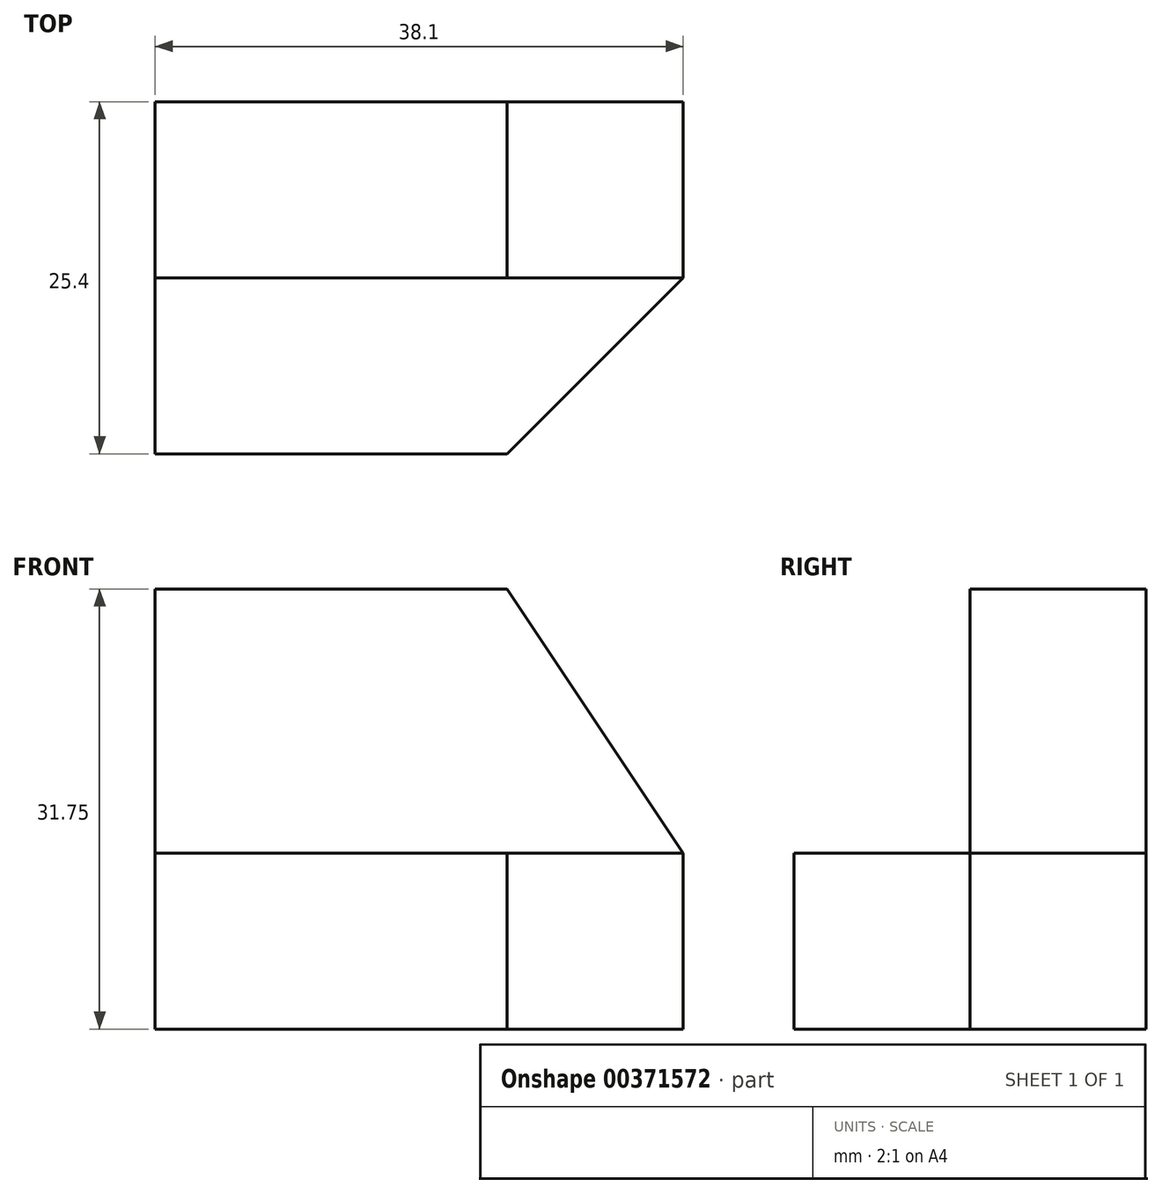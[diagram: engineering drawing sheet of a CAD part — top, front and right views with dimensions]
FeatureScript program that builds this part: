
annotation { "Feature Type Name" : "Feature", "Feature Type Description" : "" }
export const myFeature = defineFeature(function(context is Context, id is Id, definition is map)
    precondition{}
    {
        {
            var Q0;
            Q0=qCreatedBy(makeId("Right.planeOp"),FACE);
            var sketch = newSketch(context, id + "F0", { "sketchPlane" : qUnion([Q0])});
            skLineSegment(sketch, "E0", {"start": v(0, 0) * mm, "end": v(0, 19.05) * mm});
            skLineSegment(sketch, "E1", {"start": v(0, 19.05) * mm, "end": v(12.7, 19.05) * mm});
            skLineSegment(sketch, "E2", {"start": v(12.7, 19.05) * mm, "end": v(12.7, -12.7) * mm});
            skLineSegment(sketch, "E3", {"start": v(12.7, -12.7) * mm, "end": v(-12.7, -12.7) * mm});
            skLineSegment(sketch, "E4", {"start": v(-12.7, -12.7) * mm, "end": v(-12.7, 0) * mm});
            skLineSegment(sketch, "E5", {"start": v(-12.7, 0) * mm, "end": v(0, 0) * mm});
            skSolve(sketch);
        }
        {
            var Q0;
            Q0 = qSketchRegion(id + "F0", true);
            extrude(context, id + "F1", {"entities" : qUnion([Q0]), "depth" : 38.1 * mm});
        }
        {
            var Q0;
            Q0=makeQuery(id+"F1.opExtrude","SWEPT_FACE",FACE,{"disambiguationData":[OSD([sQuery(id+"F0.wireOp",EDGE,"E5")])]});
            var sketch = newSketch(context, id + "F2", { "sketchPlane" : qUnion([Q0])});
            skLineSegment(sketch, "E6", {"start": v(38.1, 0) * mm, "end": v(25.4, -12.7) * mm});
            skSolve(sketch);
        }
        {
            var Q0;
            Q0=makeQuery(id+"F1.opExtrude","SWEPT_FACE",FACE,{"disambiguationData":[OSD([sQuery(id+"F0.wireOp",EDGE,"E0")])]});
            var sketch = newSketch(context, id + "F3", { "sketchPlane" : qUnion([Q0])});
            skLineSegment(sketch, "E7", {"start": v(38.1, 0) * mm, "end": v(25.4, 19.05) * mm});
            skSolve(sketch);
        }
        {
            var Q0;
            Q0 = qSketchRegion(id + "F3", true);
            var Q1;
            Q1 = qSketchRegion(id + "F2", true);
            var Q2;
            {var subQ0=sQuery(id+"F3.wireOp",EDGE,"E7");Q2=makeQuery(id+"F3.imprint","IMPRINT",FACE,{"disambiguationData":[TD([[makeQuery(id+"F3.imprint","IMPRINT",EDGE,{"derivedFrom":subQ0}),-1.0]])]});}
            extrude(context, id + "F4", {"entities" : qUnion([Q0, Q1, Q2]), "operationType" : NewBodyOperationType.REMOVE, "oppositeDirection" : true, "depth" : 25.4 * mm});
        }
        {
            var Q0;
            Q0 = qSketchRegion(id + "F2", true);
            var Q1;
            {var subQ0=sQuery(id+"F2.wireOp",EDGE,"E6");Q1=makeQuery(id+"F2.imprint","IMPRINT",FACE,{"disambiguationData":[TD([[makeQuery(id+"F2.imprint","IMPRINT",EDGE,{"derivedFrom":subQ0}),1.0]])]});}
            extrude(context, id + "F5", {"entities" : qUnion([Q0, Q1]), "operationType" : NewBodyOperationType.REMOVE, "oppositeDirection" : true, "depth" : 25.4 * mm});
        }
    });
